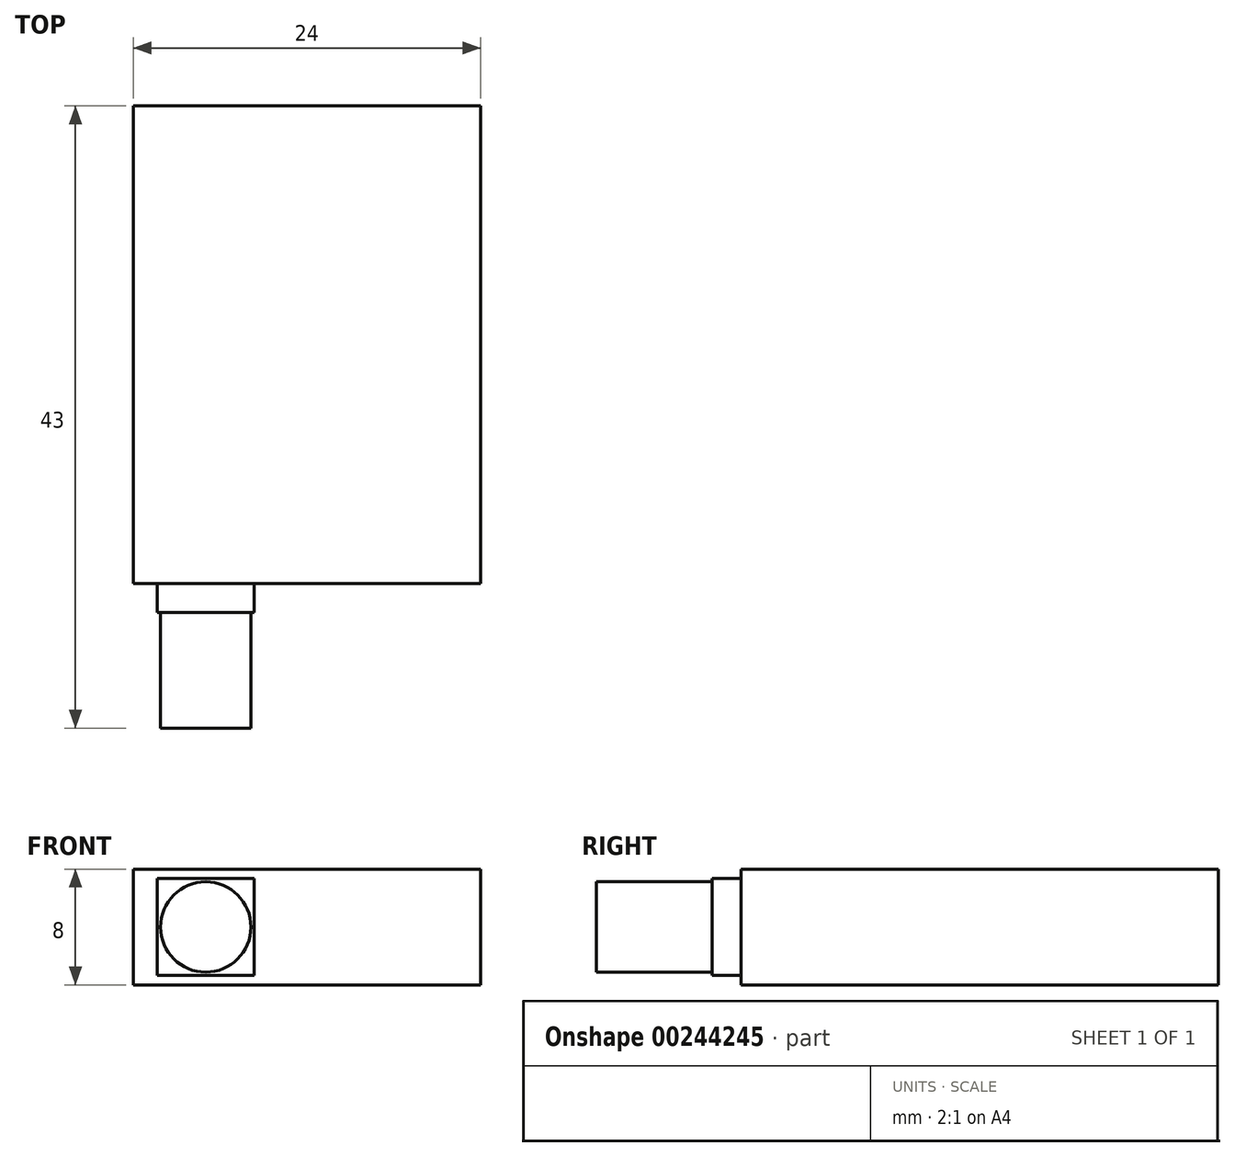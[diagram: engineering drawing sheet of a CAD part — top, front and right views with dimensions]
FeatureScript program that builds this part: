
annotation { "Feature Type Name" : "Feature", "Feature Type Description" : "" }
export const myFeature = defineFeature(function(context is Context, id is Id, definition is map)
    precondition{}
    {
        {
            var Q0;
            Q0=qCreatedBy(makeId("Top.planeOp"),FACE);
            var sketch = newSketch(context, id + "F0", { "sketchPlane" : qUnion([Q0])});
            skLineSegment(sketch, "E0.bottom", {"start": v(12, 16.5) * mm, "end": v(-12, 16.5) * mm});
            skLineSegment(sketch, "E0.top", {"start": v(12, -16.5) * mm, "end": v(-12, -16.5) * mm});
            skLineSegment(sketch, "E0.left", {"start": v(12, 16.5) * mm, "end": v(12, -16.5) * mm});
            skLineSegment(sketch, "E0.right", {"start": v(-12, 16.5) * mm, "end": v(-12, -16.5) * mm});
            skPoint(sketch, "E0.middle", {"position": v(0, 0) * mm});
            skSolve(sketch);
        }
        {
            var Q0;
            Q0=qSketchRegion(id+"F0",true);
            extrude(context, id + "F1", {"entities" : qUnion([Q0]), "depth" : 8 * mm});
        }
        {
            var Q0;
            Q0=makeQuery(id+"F1.opExtrude","SWEPT_FACE",FACE,{"disambiguationData":[OSD([sQuery(id+"F0.wireOp",EDGE,"E0.top")])]});
            var sketch = newSketch(context, id + "F2", { "sketchPlane" : qUnion([Q0])});
            skLineSegment(sketch, "E1.bottom", {"start": v(-3.65, 0.65) * mm, "end": v(-10.35, 0.65) * mm});
            skLineSegment(sketch, "E1.top", {"start": v(-3.65, 7.35) * mm, "end": v(-10.35, 7.35) * mm});
            skLineSegment(sketch, "E1.left", {"start": v(-3.65, 0.65) * mm, "end": v(-3.65, 7.35) * mm});
            skLineSegment(sketch, "E1.right", {"start": v(-10.35, 0.65) * mm, "end": v(-10.35, 7.35) * mm});
            skPoint(sketch, "E1.middle", {"position": v(-7, 4) * mm});
            skLineSegment(sketch, "E2", {"start": v(-12, 4) * mm, "end": v(-7, 4) * mm, "construction": true});
            skSolve(sketch);
        }
        {
            var Q0;
            Q0=qSketchRegion(id+"F2",true);
            extrude(context, id + "F3", {"entities" : qUnion([Q0]), "operationType" : NewBodyOperationType.ADD, "depth" : 2 * mm});
        }
        {
            var Q0;
            Q0=makeQuery(id+"F3.opExtrude","CAP_FACE",FACE,{"disambiguationData":[OSD([sQuery(id+"F2.wireOp",EDGE,"E1.bottom"),sQuery(id+"F2.wireOp",EDGE,"E1.top"),sQuery(id+"F2.wireOp",EDGE,"E1.left"),sQuery(id+"F2.wireOp",EDGE,"E1.right")])],"isStart":false});
            var sketch = newSketch(context, id + "F4", { "sketchPlane" : qUnion([Q0])});
            skLineSegment(sketch, "E3", {"start": v(-10.35, 7.35) * mm, "end": v(-3.65, 0.65) * mm, "construction": true});
            skCircle(sketch, "E4", {"center": v(-7, 4) * mm, "radius": 3.12 * mm});
            skSolve(sketch);
        }
        {
            var Q0;
            Q0=qSketchRegion(id+"F4",true);
            extrude(context, id + "F5", {"entities" : qUnion([Q0]), "operationType" : NewBodyOperationType.ADD, "depth" : 8 * mm});
        }
    });
